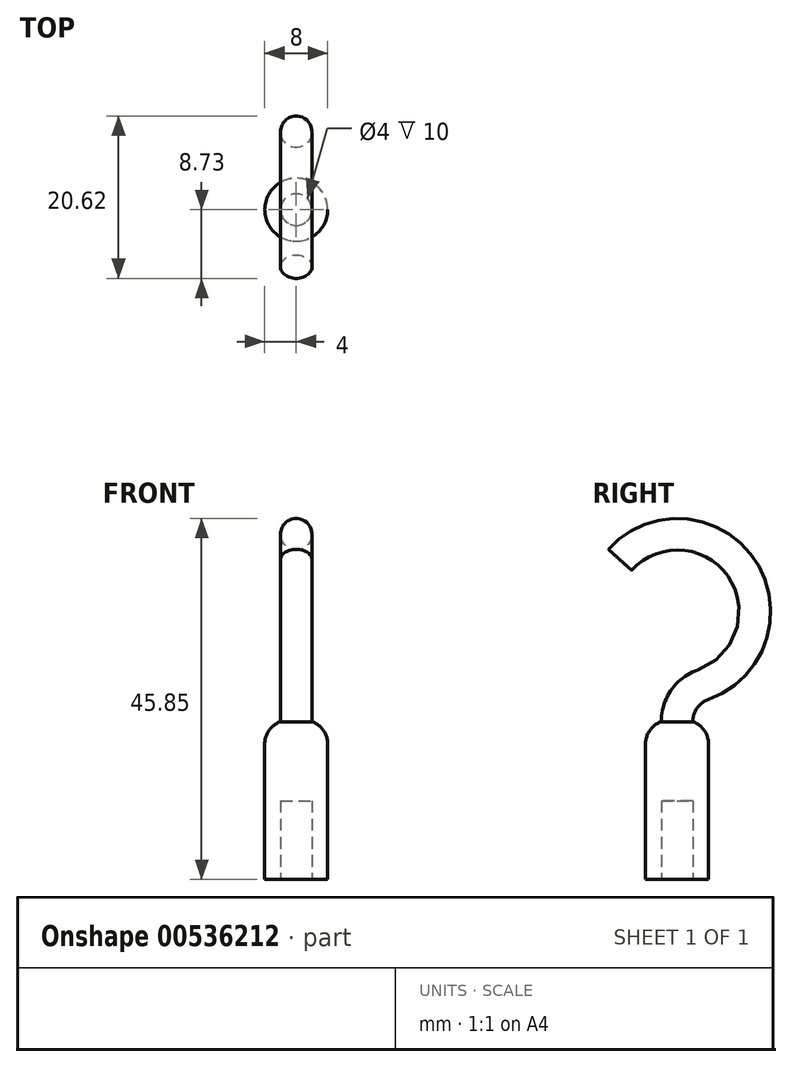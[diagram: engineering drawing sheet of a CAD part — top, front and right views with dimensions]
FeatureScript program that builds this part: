
annotation { "Feature Type Name" : "Feature", "Feature Type Description" : "" }
export const myFeature = defineFeature(function(context is Context, id is Id, definition is map)
    precondition{}
    {
        {
            var Q0;
            Q0=qCreatedBy(makeId("Top.planeOp"),FACE);
            var sketch = newSketch(context, id + "F0", { "sketchPlane" : qUnion([Q0])});
            skCircle(sketch, "E0", {"center": v(0, 0) * mm, "radius": 4 * mm});
            skSolve(sketch);
        }
        {
            var Q0;
            Q0=qCreatedBy(makeId("Right.planeOp"),FACE);
            var sketch = newSketch(context, id + "F1", { "sketchPlane" : qUnion([Q0])});
            skLineSegment(sketch, "E1", {"start": v(0, 0) * mm, "end": v(0, 20.04) * mm});
            skArc(sketch, "E2", {"start": v(3.34, 24.75) * mm, "mid": v(8.24, 39.48) * mm, "end": v(-7.24, 40.6) * mm});
            skPoint(sketch, "E3.visualSharp", {"position": v(0, 24.2) * mm});
            skArc(sketch, "E3.filletArc", {"start": v(3.34, 24.75) * mm, "mid": v(0.92, 22.92) * mm, "end": v(0, 20.04) * mm});
            skSolve(sketch);
        }
        {
            var Q0;
            Q0=makeQuery(id+"F0.imprint","IMPRINT",FACE,{"disambiguationData":[TD([[makeQuery(id+"F0.imprint","IMPRINT",EDGE,{"derivedFrom":sQuery(id+"F0.wireOp",EDGE,"E0")}),1.0]])]});
            var Q1;
            Q1=sQuery(id+"F1.wireOp",EDGE,"E1");
            sweep(context, id + "F2", {"profiles" : qUnion([Q0]), "path" : qUnion([Q1])});
        }
        {
            var Q0;
            Q0=makeQuery(id+"F2.opSweep","CAP_FACE",FACE,{"disambiguationData":[OSD([sQuery(id+"F0.wireOp",EDGE,"E0"),sQuery(id+"F1.wireOp",VERTEX,"E1.end")])],"isStart":false});
            var sketch = newSketch(context, id + "F3", { "sketchPlane" : qUnion([Q0])});
            skCircle(sketch, "E4", {"center": v(0, 0) * mm, "radius": 2 * mm});
            skSolve(sketch);
        }
        {
            var Q0;
            Q0=makeQuery(id+"F3.imprint","IMPRINT",FACE,{"disambiguationData":[TD([[makeQuery(id+"F3.imprint","IMPRINT",EDGE,{"derivedFrom":sQuery(id+"F3.wireOp",EDGE,"E4")}),1.0]])]});
            var Q1;
            Q1=sQuery(id+"F1.wireOp",EDGE,"E3.filletArc");
            var Q2;
            Q2=sQuery(id+"F1.wireOp",EDGE,"E2");
            sweep(context, id + "F4", {"operationType" : NewBodyOperationType.ADD, "profiles" : qUnion([Q0]), "path" : qUnion([Q1, Q2])});
        }
        {
            var Q0;
            Q0=makeQuery(id+"F2.opSweep","CAP_EDGE",EDGE,{"disambiguationData":[OSD([sQuery(id+"F0.wireOp",EDGE,"E0"),sQuery(id+"F1.wireOp",VERTEX,"E1.end")])],"isStart":false});
            fillet(context, id + "F5", {"entities" : qUnion([Q0]), "radius" : 3 * mm, "tangentPropagation" : true, "allowEdgeOverflow" : false});
        }
        {
            var Q0;
            Q0=makeQuery(id+"F2.opSweep","CAP_FACE",FACE,{"disambiguationData":[OSD([sQuery(id+"F0.wireOp",EDGE,"E0"),sQuery(id+"F1.wireOp",VERTEX,"E1.start")])],"isStart":true});
            var sketch = newSketch(context, id + "F6", { "sketchPlane" : qUnion([Q0])});
            skCircle(sketch, "E5", {"center": v(0, 0) * mm, "radius": 2 * mm});
            skSolve(sketch);
        }
        {
            var Q0;
            Q0=makeQuery(id+"F6.imprint","IMPRINT",FACE,{"disambiguationData":[TD([[makeQuery(id+"F6.imprint","IMPRINT",EDGE,{"derivedFrom":sQuery(id+"F6.wireOp",EDGE,"E5")}),1.0]])]});
            extrude(context, id + "F7", {"entities" : qUnion([Q0]), "operationType" : NewBodyOperationType.REMOVE, "oppositeDirection" : true, "depth" : 10 * mm, "offsetDistance" : 25 * mm});
        }
    });
